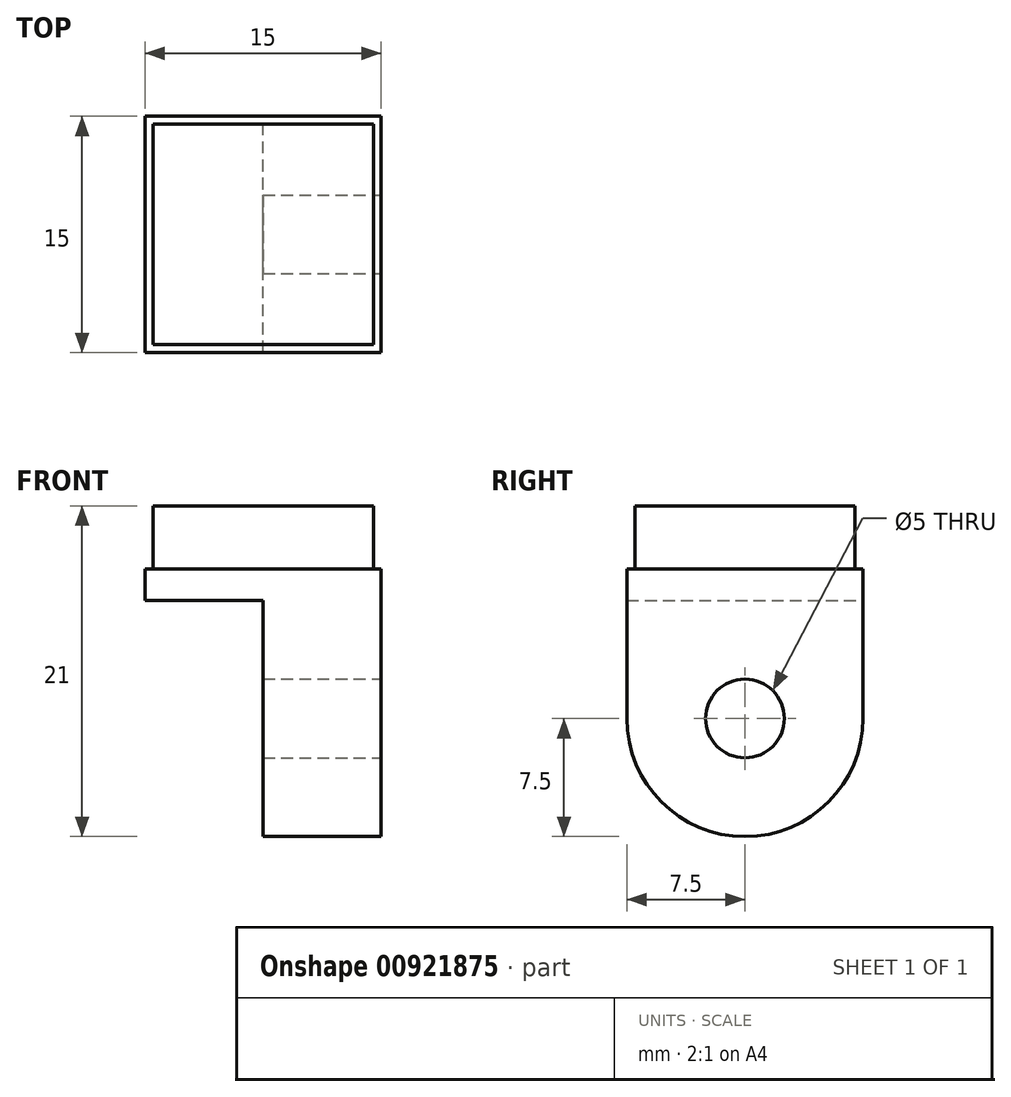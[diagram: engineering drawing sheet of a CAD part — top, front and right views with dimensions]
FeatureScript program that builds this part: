
annotation { "Feature Type Name" : "Feature", "Feature Type Description" : "" }
export const myFeature = defineFeature(function(context is Context, id is Id, definition is map)
    precondition{}
    {
        {
            var Q0;
            Q0=qCreatedBy(makeId("Top.planeOp"),FACE);
            var sketch = newSketch(context, id + "F0", { "sketchPlane" : qUnion([Q0])});
            skLineSegment(sketch, "E0.bottom", {"start": v(7.5, -7.5) * mm, "end": v(-7.5, -7.5) * mm});
            skLineSegment(sketch, "E0.top", {"start": v(7.5, 7.5) * mm, "end": v(-7.5, 7.5) * mm});
            skLineSegment(sketch, "E0.left", {"start": v(7.5, -7.5) * mm, "end": v(7.5, 7.5) * mm});
            skLineSegment(sketch, "E0.right", {"start": v(-7.5, -7.5) * mm, "end": v(-7.5, 7.5) * mm});
            skPoint(sketch, "E0.middle", {"position": v(0, 0) * mm});
            skLineSegment(sketch, "E1.bottom", {"start": v(7, -7) * mm, "end": v(-7, -7) * mm});
            skLineSegment(sketch, "E1.top", {"start": v(7, 7) * mm, "end": v(-7, 7) * mm});
            skLineSegment(sketch, "E1.left", {"start": v(7, -7) * mm, "end": v(7, 7) * mm});
            skLineSegment(sketch, "E1.right", {"start": v(-7, -7) * mm, "end": v(-7, 7) * mm});
            skSolve(sketch);
        }
        {
            var Q0;
            Q0=makeQuery(id+"F0.imprint","IMPRINT",FACE,{"disambiguationData":[TD([[makeQuery(id+"F0.imprint","IMPRINT",EDGE,{"derivedFrom":sQuery(id+"F0.wireOp",EDGE,"E0.bottom")}),-1.0]])]});
            extrude(context, id + "F1", {"entities" : qUnion([Q0]), "depth" : 2 * mm, "offsetDistance" : 25 * mm});
        }
        {
            var Q0;
            Q0=makeQuery(id+"F0.imprint","IMPRINT",FACE,{"disambiguationData":[TD([[makeQuery(id+"F0.imprint","IMPRINT",EDGE,{"derivedFrom":sQuery(id+"F0.wireOp",EDGE,"E1.bottom")}),-1.0]])]});
            extrude(context, id + "F2", {"entities" : qUnion([Q0]), "operationType" : NewBodyOperationType.ADD, "depth" : 6 * mm, "offsetDistance" : 25 * mm});
        }
        {
            var Q0;
            {var subQ0=sQuery(id+"F0.wireOp",EDGE,"E1.right");var subQ1=sQuery(id+"F0.wireOp",EDGE,"E1.left");var subQ2=sQuery(id+"F0.wireOp",EDGE,"E1.top");var subQ3=sQuery(id+"F0.wireOp",EDGE,"E1.bottom");Q0=makeQuery(id+"F2.boolean.opBoolean","MERGE",FACE,{"derivedFrom":[makeQuery(id+"F1.opExtrude","CAP_FACE",FACE,{"disambiguationData":[OSD([sQuery(id+"F0.wireOp",EDGE,"E0.bottom"),sQuery(id+"F0.wireOp",EDGE,"E0.top"),sQuery(id+"F0.wireOp",EDGE,"E0.left"),sQuery(id+"F0.wireOp",EDGE,"E0.right"),subQ3,subQ2,subQ1,subQ0])],"isStart":true}),makeQuery(id+"F2.opExtrude","CAP_FACE",FACE,{"disambiguationData":[OSD([subQ3,subQ2,subQ1,subQ0])],"isStart":true})]});}
            var sketch = newSketch(context, id + "F3", { "sketchPlane" : qUnion([Q0])});
            skLineSegment(sketch, "E2.bottom", {"start": v(0, 7.5) * mm, "end": v(7.5, 7.5) * mm});
            skLineSegment(sketch, "E2.top", {"start": v(0, -7.5) * mm, "end": v(7.5, -7.5) * mm});
            skLineSegment(sketch, "E2.left", {"start": v(0, 7.5) * mm, "end": v(0, -7.5) * mm});
            skLineSegment(sketch, "E2.right", {"start": v(7.5, 7.5) * mm, "end": v(7.5, -7.5) * mm});
            skSolve(sketch);
        }
        {
            var Q0;
            Q0=makeQuery(id+"F3.imprint","IMPRINT",FACE,{"disambiguationData":[TD([[makeQuery(id+"F3.imprint","IMPRINT",EDGE,{"derivedFrom":sQuery(id+"F3.wireOp",EDGE,"E2.bottom")}),1.0]])]});
            extrude(context, id + "F4", {"entities" : qUnion([Q0]), "operationType" : NewBodyOperationType.ADD, "depth" : 15 * mm, "offsetDistance" : 25 * mm});
        }
        {
            var Q0;
            Q0=makeQuery(id+"F4.opExtrude","CAP_EDGE",EDGE,{"disambiguationData":[OSD([sQuery(id+"F3.wireOp",EDGE,"E2.top")])],"isStart":false});
            var Q1;
            Q1=makeQuery(id+"F4.opExtrude","CAP_EDGE",EDGE,{"disambiguationData":[OSD([sQuery(id+"F3.wireOp",EDGE,"E2.bottom")])],"isStart":false});
            fillet(context, id + "F5", {"entities" : qUnion([Q0, Q1]), "radius" : 7.5 * mm, "tangentPropagation" : true, "allowEdgeOverflow" : false});
        }
        {
            var Q0;
            Q0=makeQuery(id+"F4.boolean.opBoolean","MERGE",FACE,{"derivedFrom":[makeQuery(id+"F1.opExtrude","SWEPT_FACE",FACE,{"disambiguationData":[OSD([sQuery(id+"F0.wireOp",EDGE,"E0.left")])]}),makeQuery(id+"F4.opExtrude","SWEPT_FACE",FACE,{"disambiguationData":[OSD([sQuery(id+"F3.wireOp",EDGE,"E2.right")])]})]});
            var sketch = newSketch(context, id + "F6", { "sketchPlane" : qUnion([Q0])});
            skCircle(sketch, "E3", {"center": v(0, -7.5) * mm, "radius": 2.5 * mm});
            skSolve(sketch);
        }
        {
            var Q0;
            Q0=makeQuery(id+"F6.imprint","IMPRINT",FACE,{"disambiguationData":[TD([[makeQuery(id+"F6.imprint","IMPRINT",EDGE,{"derivedFrom":sQuery(id+"F6.wireOp",EDGE,"E3")}),1.0]])]});
            extrude(context, id + "F7", {"entities" : qUnion([Q0]), "operationType" : NewBodyOperationType.REMOVE, "oppositeDirection" : true, "depth" : 25 * mm, "offsetDistance" : 25 * mm});
        }
    });
